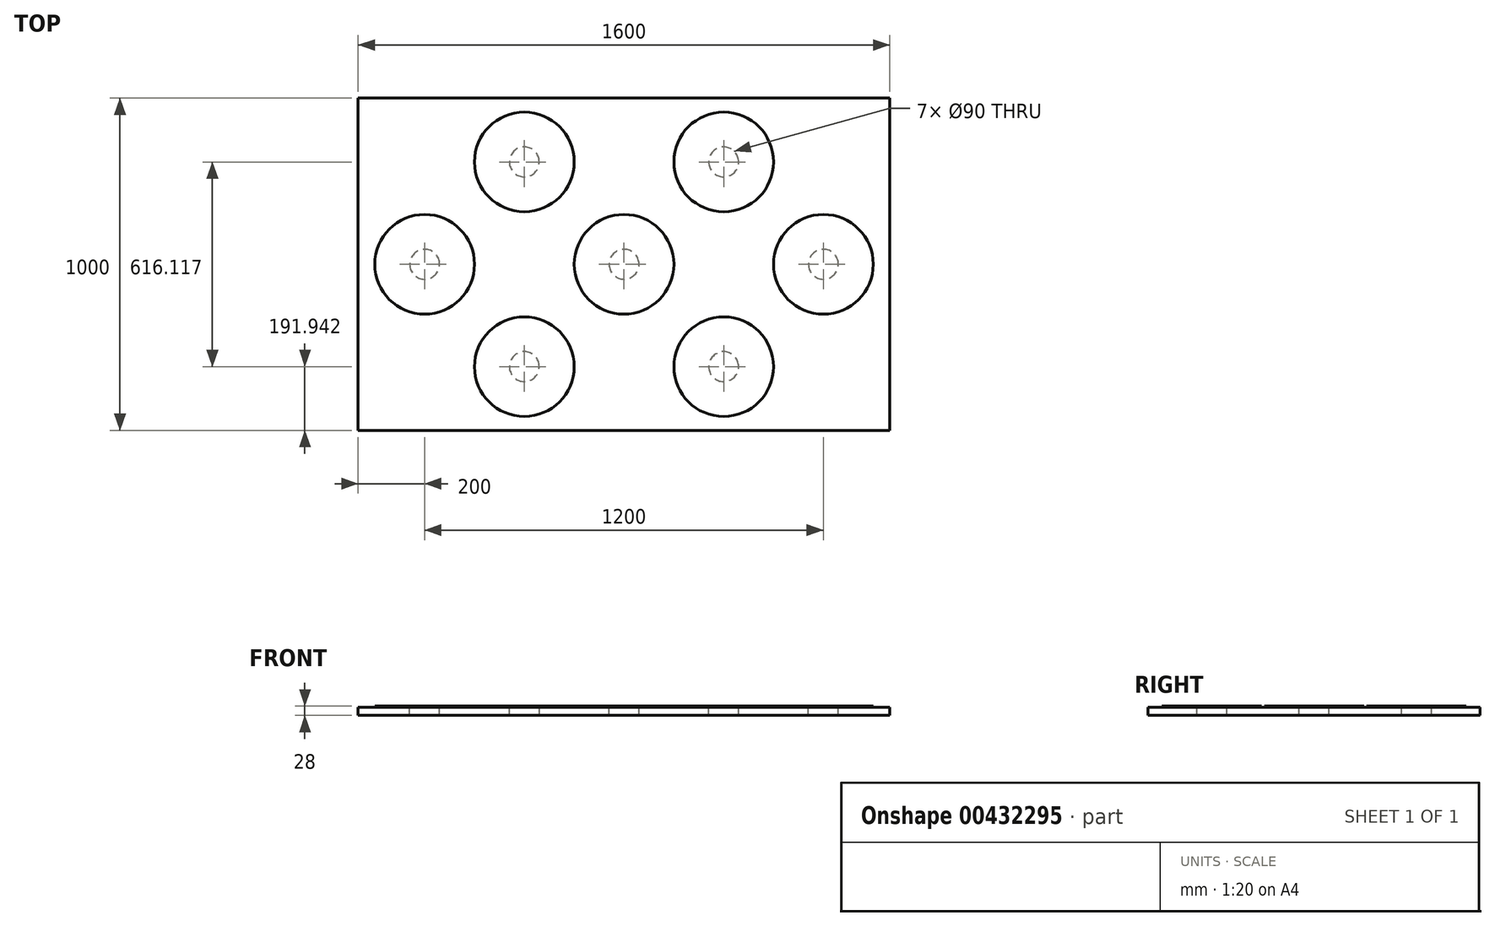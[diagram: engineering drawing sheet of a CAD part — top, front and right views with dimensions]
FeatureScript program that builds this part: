
annotation { "Feature Type Name" : "Feature", "Feature Type Description" : "" }
export const myFeature = defineFeature(function(context is Context, id is Id, definition is map)
    precondition{}
    {
        {
            var Q0;
            Q0=qCreatedBy(makeId("Top.planeOp"),FACE);
            var sketch = newSketch(context, id + "F0", { "sketchPlane" : qUnion([Q0])});
            skLineSegment(sketch, "E0.bottom", {"start": v(800, 500) * mm, "end": v(-800, 500) * mm});
            skLineSegment(sketch, "E0.top", {"start": v(800, -500) * mm, "end": v(-800, -500) * mm});
            skLineSegment(sketch, "E0.left", {"start": v(800, 500) * mm, "end": v(800, -500) * mm});
            skLineSegment(sketch, "E0.right", {"start": v(-800, 500) * mm, "end": v(-800, -500) * mm});
            skPoint(sketch, "E0.middle", {"position": v(0, 0) * mm});
            skSolve(sketch);
        }
        {
            var Q0;
            Q0=makeQuery(id+"F0.imprint","IMPRINT",FACE,{"disambiguationData":[TD([[makeQuery(id+"F0.imprint","IMPRINT",EDGE,{"derivedFrom":sQuery(id+"F0.wireOp",EDGE,"E0.bottom")}),1.0]])]});
            extrude(context, id + "F1", {"entities" : qUnion([Q0]), "depth" : 25 * mm});
        }
        {
            var Q0;
            Q0=makeQuery(id+"F1.opExtrude","CAP_FACE",FACE,{"disambiguationData":[OSD([sQuery(id+"F0.wireOp",EDGE,"E0.bottom"),sQuery(id+"F0.wireOp",EDGE,"E0.top"),sQuery(id+"F0.wireOp",EDGE,"E0.left"),sQuery(id+"F0.wireOp",EDGE,"E0.right")])],"isStart":false});
            var sketch = newSketch(context, id + "F2", { "sketchPlane" : qUnion([Q0])});
            skCircle(sketch, "E1", {"center": v(0, 0) * mm, "radius": 45 * mm});
            skLineSegment(sketch, "E2", {"start": v(600, 0) * mm, "end": v(-600, 0) * mm, "construction": true});
            skLineSegment(sketch, "E3", {"start": v(-300, 308.06) * mm, "end": v(300, 308.06) * mm, "construction": true});
            skLineSegment(sketch, "E4", {"start": v(300, 308.06) * mm, "end": v(600, 0) * mm, "construction": true});
            skLineSegment(sketch, "E5", {"start": v(600, 0) * mm, "end": v(300, -308.06) * mm, "construction": true});
            skLineSegment(sketch, "E6", {"start": v(300, -308.06) * mm, "end": v(-300, -308.06) * mm, "construction": true});
            skLineSegment(sketch, "E7", {"start": v(-300, -308.06) * mm, "end": v(-600, 0) * mm, "construction": true});
            skLineSegment(sketch, "E8", {"start": v(-300, 308.06) * mm, "end": v(-600, 0) * mm, "construction": true});
            skCircle(sketch, "E9", {"center": v(300, -308.06) * mm, "radius": 45 * mm});
            skCircle(sketch, "E10", {"center": v(-300, -308.06) * mm, "radius": 45 * mm});
            skCircle(sketch, "E11", {"center": v(-600, 0) * mm, "radius": 45 * mm});
            skCircle(sketch, "E12", {"center": v(-300, 308.06) * mm, "radius": 45 * mm});
            skCircle(sketch, "E13", {"center": v(300, 308.06) * mm, "radius": 45 * mm});
            skCircle(sketch, "E14", {"center": v(600, 0) * mm, "radius": 45 * mm});
            skCircle(sketch, "E15", {"center": v(-300, 308.06) * mm, "radius": 150 * mm});
            skCircle(sketch, "E16", {"center": v(-600, 0) * mm, "radius": 150 * mm});
            skCircle(sketch, "E17", {"center": v(0, 0) * mm, "radius": 150 * mm});
            skCircle(sketch, "E18", {"center": v(300, 308.06) * mm, "radius": 150 * mm});
            skCircle(sketch, "E19", {"center": v(600, 0) * mm, "radius": 150 * mm});
            skCircle(sketch, "E20", {"center": v(300, -308.06) * mm, "radius": 150 * mm});
            skCircle(sketch, "E21", {"center": v(-300, -308.06) * mm, "radius": 150 * mm});
            skSolve(sketch);
        }
        {
            var Q0;
            Q0=makeQuery(id+"F2.imprint","IMPRINT",FACE,{"disambiguationData":[TD([[makeQuery(id+"F2.imprint","IMPRINT",EDGE,{"derivedFrom":sQuery(id+"F2.wireOp",EDGE,"E11")}),1.0]])]});
            var Q1;
            Q1=makeQuery(id+"F2.imprint","IMPRINT",FACE,{"disambiguationData":[TD([[makeQuery(id+"F2.imprint","IMPRINT",EDGE,{"derivedFrom":sQuery(id+"F2.wireOp",EDGE,"E12")}),1.0]])]});
            var Q2;
            Q2=makeQuery(id+"F2.imprint","IMPRINT",FACE,{"disambiguationData":[TD([[makeQuery(id+"F2.imprint","IMPRINT",EDGE,{"derivedFrom":sQuery(id+"F2.wireOp",EDGE,"E13")}),1.0]])]});
            var Q3;
            Q3=makeQuery(id+"F2.imprint","IMPRINT",FACE,{"disambiguationData":[TD([[makeQuery(id+"F2.imprint","IMPRINT",EDGE,{"derivedFrom":sQuery(id+"F2.wireOp",EDGE,"E14")}),1.0]])]});
            var Q4;
            Q4=makeQuery(id+"F2.imprint","IMPRINT",FACE,{"disambiguationData":[TD([[makeQuery(id+"F2.imprint","IMPRINT",EDGE,{"derivedFrom":sQuery(id+"F2.wireOp",EDGE,"E1")}),1.0]])]});
            var Q5;
            Q5=makeQuery(id+"F2.imprint","IMPRINT",FACE,{"disambiguationData":[TD([[makeQuery(id+"F2.imprint","IMPRINT",EDGE,{"derivedFrom":sQuery(id+"F2.wireOp",EDGE,"E9")}),1.0]])]});
            var Q6;
            Q6=makeQuery(id+"F2.imprint","IMPRINT",FACE,{"disambiguationData":[TD([[makeQuery(id+"F2.imprint","IMPRINT",EDGE,{"derivedFrom":sQuery(id+"F2.wireOp",EDGE,"E10")}),1.0]])]});
            extrude(context, id + "F3", {"entities" : qUnion([Q0, Q1, Q2, Q3, Q4, Q5, Q6]), "operationType" : NewBodyOperationType.REMOVE, "oppositeDirection" : true, "depth" : 25 * mm});
        }
        {
            var Q0;
            Q0=makeQuery(id+"F2.imprint","IMPRINT",FACE,{"disambiguationData":[TD([[makeQuery(id+"F2.imprint","IMPRINT",EDGE,{"derivedFrom":sQuery(id+"F2.wireOp",EDGE,"E11")}),-1.0]])]});
            var Q1;
            Q1=makeQuery(id+"F2.imprint","IMPRINT",FACE,{"disambiguationData":[TD([[makeQuery(id+"F2.imprint","IMPRINT",EDGE,{"derivedFrom":sQuery(id+"F2.wireOp",EDGE,"E12")}),-1.0]])]});
            var Q2;
            Q2=makeQuery(id+"F2.imprint","IMPRINT",FACE,{"disambiguationData":[TD([[makeQuery(id+"F2.imprint","IMPRINT",EDGE,{"derivedFrom":sQuery(id+"F2.wireOp",EDGE,"E1")}),-1.0]])]});
            var Q3;
            Q3=makeQuery(id+"F2.imprint","IMPRINT",FACE,{"disambiguationData":[TD([[makeQuery(id+"F2.imprint","IMPRINT",EDGE,{"derivedFrom":sQuery(id+"F2.wireOp",EDGE,"E13")}),-1.0]])]});
            var Q4;
            Q4=makeQuery(id+"F2.imprint","IMPRINT",FACE,{"disambiguationData":[TD([[makeQuery(id+"F2.imprint","IMPRINT",EDGE,{"derivedFrom":sQuery(id+"F2.wireOp",EDGE,"E12")}),1.0]])]});
            var Q5;
            Q5=makeQuery(id+"F2.imprint","IMPRINT",FACE,{"disambiguationData":[TD([[makeQuery(id+"F2.imprint","IMPRINT",EDGE,{"derivedFrom":sQuery(id+"F2.wireOp",EDGE,"E13")}),1.0]])]});
            var Q6;
            Q6=makeQuery(id+"F2.imprint","IMPRINT",FACE,{"disambiguationData":[TD([[makeQuery(id+"F2.imprint","IMPRINT",EDGE,{"derivedFrom":sQuery(id+"F2.wireOp",EDGE,"E9")}),-1.0]])]});
            var Q7;
            Q7=makeQuery(id+"F2.imprint","IMPRINT",FACE,{"disambiguationData":[TD([[makeQuery(id+"F2.imprint","IMPRINT",EDGE,{"derivedFrom":sQuery(id+"F2.wireOp",EDGE,"E9")}),1.0]])]});
            var Q8;
            Q8=makeQuery(id+"F2.imprint","IMPRINT",FACE,{"disambiguationData":[TD([[makeQuery(id+"F2.imprint","IMPRINT",EDGE,{"derivedFrom":sQuery(id+"F2.wireOp",EDGE,"E10")}),-1.0]])]});
            var Q9;
            Q9=makeQuery(id+"F2.imprint","IMPRINT",FACE,{"disambiguationData":[TD([[makeQuery(id+"F2.imprint","IMPRINT",EDGE,{"derivedFrom":sQuery(id+"F2.wireOp",EDGE,"E10")}),1.0]])]});
            var Q10;
            Q10=makeQuery(id+"F2.imprint","IMPRINT",FACE,{"disambiguationData":[TD([[makeQuery(id+"F2.imprint","IMPRINT",EDGE,{"derivedFrom":sQuery(id+"F2.wireOp",EDGE,"E1")}),1.0]])]});
            var Q11;
            Q11=makeQuery(id+"F2.imprint","IMPRINT",FACE,{"disambiguationData":[TD([[makeQuery(id+"F2.imprint","IMPRINT",EDGE,{"derivedFrom":sQuery(id+"F2.wireOp",EDGE,"E11")}),1.0]])]});
            var Q12;
            Q12=makeQuery(id+"F2.imprint","IMPRINT",FACE,{"disambiguationData":[TD([[makeQuery(id+"F2.imprint","IMPRINT",EDGE,{"derivedFrom":sQuery(id+"F2.wireOp",EDGE,"E14")}),1.0]])]});
            var Q13;
            Q13=makeQuery(id+"F2.imprint","IMPRINT",FACE,{"disambiguationData":[TD([[makeQuery(id+"F2.imprint","IMPRINT",EDGE,{"derivedFrom":sQuery(id+"F2.wireOp",EDGE,"E14")}),-1.0]])]});
            extrude(context, id + "F4", {"entities" : qUnion([Q0, Q1, Q2, Q3, Q4, Q5, Q6, Q7, Q8, Q9, Q10, Q11, Q12, Q13]), "depth" : 3 * mm});
        }
    });
